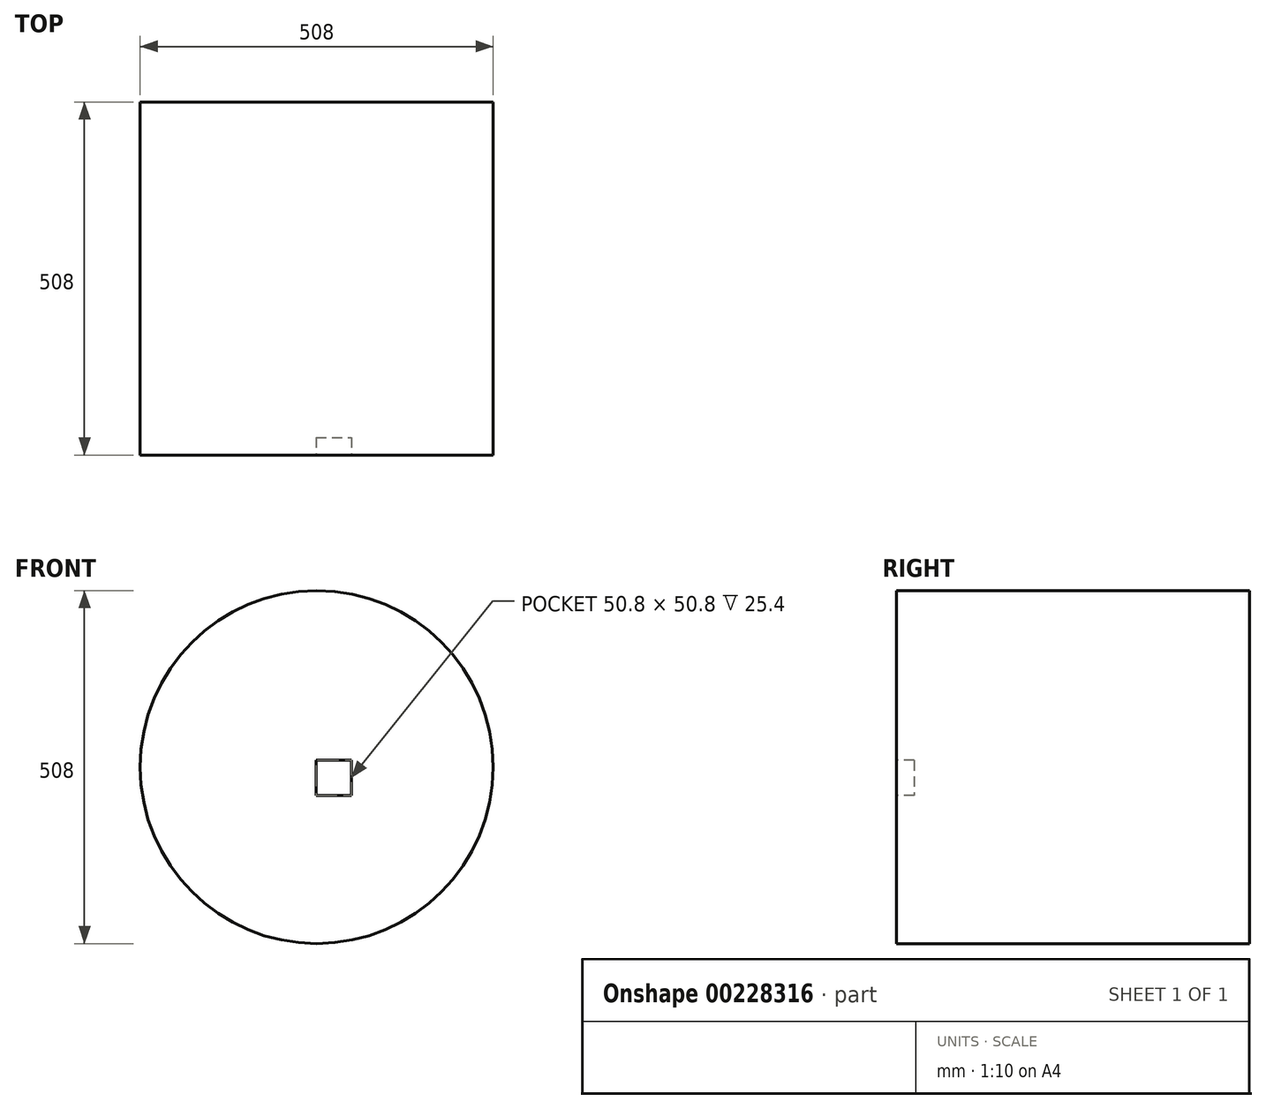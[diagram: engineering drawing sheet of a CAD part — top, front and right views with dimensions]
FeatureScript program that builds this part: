
annotation { "Feature Type Name" : "Feature", "Feature Type Description" : "" }
export const myFeature = defineFeature(function(context is Context, id is Id, definition is map)
    precondition{}
    {
        {
            var Q0;
            Q0=qCreatedBy(makeId("Front.planeOp"),FACE);
            var sketch = newSketch(context, id + "F0", { "sketchPlane" : qUnion([Q0])});
            skCircle(sketch, "E0", {"center": v(0, 1.6) * mm, "radius": 254 * mm});
            skSolve(sketch);
        }
        {
            var Q0;
            Q0=makeQuery(id+"F0.imprint","IMPRINT",FACE,{"disambiguationData":[TD([[makeQuery(id+"F0.imprint","IMPRINT",EDGE,{"derivedFrom":sQuery(id+"F0.wireOp",EDGE,"E0")}),1.0]])]});
            extrude(context, id + "F1", {"entities" : qUnion([Q0]), "depth" : 508 * mm});
        }
        {
            var Q0;
            Q0=makeQuery(id+"F1.opExtrude","CAP_FACE",FACE,{"disambiguationData":[OSD([sQuery(id+"F0.wireOp",EDGE,"E0")])],"isStart":false});
            var sketch = newSketch(context, id + "F2", { "sketchPlane" : qUnion([Q0])});
            skLineSegment(sketch, "E1.bottom", {"start": v(-1.17, 11.25) * mm, "end": v(49.63, 11.25) * mm});
            skLineSegment(sketch, "E1.top", {"start": v(-1.17, -39.55) * mm, "end": v(49.63, -39.55) * mm});
            skLineSegment(sketch, "E1.left", {"start": v(-1.17, 11.25) * mm, "end": v(-1.17, -39.55) * mm});
            skLineSegment(sketch, "E1.right", {"start": v(49.63, 11.25) * mm, "end": v(49.63, -39.55) * mm});
            skSolve(sketch);
        }
        {
            var Q0;
            Q0 = qSketchRegion(id + "F2", true);
            extrude(context, id + "F3", {"entities" : qUnion([Q0]), "operationType" : NewBodyOperationType.REMOVE, "oppositeDirection" : true, "depth" : 25.4 * mm, "hasSecondDirection" : true, "secondDirectionBound" : SecondDirectionBoundingType.THROUGH_ALL, "secondDirectionOppositeDirection" : false, "secondDirectionDepth" : 25.4 * mm});
        }
    });
